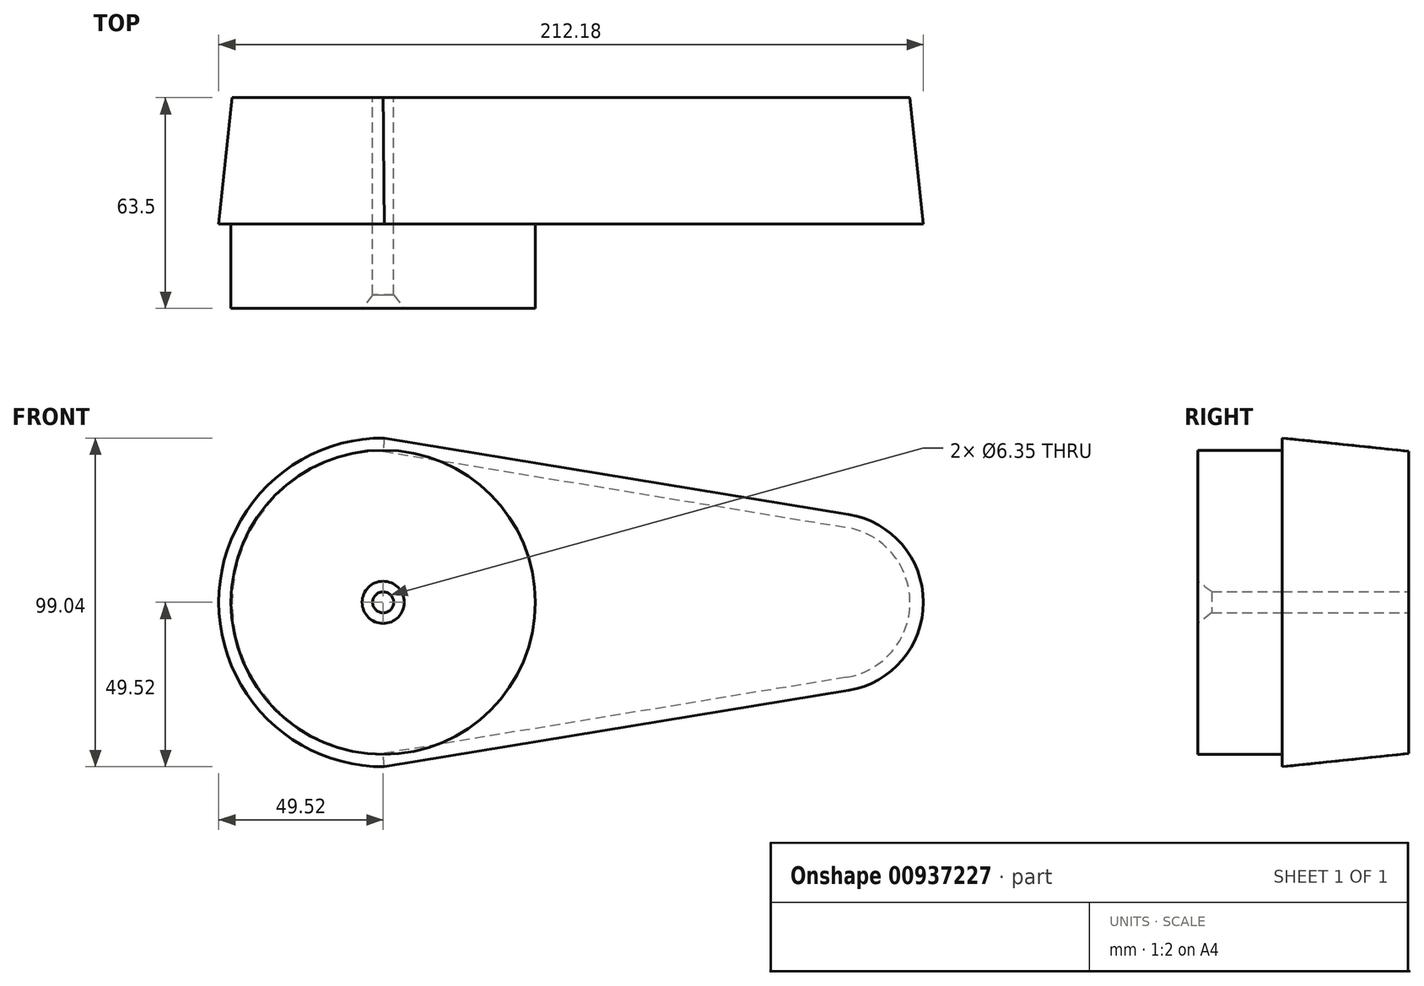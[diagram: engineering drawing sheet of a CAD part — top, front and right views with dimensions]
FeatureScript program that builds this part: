
annotation { "Feature Type Name" : "Feature", "Feature Type Description" : "" }
export const myFeature = defineFeature(function(context is Context, id is Id, definition is map)
    precondition{}
    {
        {
            var Q0;
            Q0=qCreatedBy(makeId("Front.planeOp"),FACE);
            var sketch = newSketch(context, id + "F0", { "sketchPlane" : qUnion([Q0])});
            skArc(sketch, "E0", {"start": v(139.5, -22.57) * mm, "mid": v(158.65, 0) * mm, "end": v(139.5, 22.57) * mm});
            skLineSegment(sketch, "E1", {"start": v(0, -45.52) * mm, "end": v(139.5, -22.57) * mm});
            skLineSegment(sketch, "E2", {"start": v(0, 45.52) * mm, "end": v(139.5, 22.57) * mm});
            skArc(sketch, "E3.trimOffspring", {"start": v(0, 45.52) * mm, "mid": v(-45.52, 0) * mm, "end": v(0, -45.52) * mm});
            skSolve(sketch);
        }
        {
            var Q0;
            Q0 = qSketchRegion(id + "F0", true);
            extrude(context, id + "F1", {"entities" : qUnion([Q0]), "depth" : 38.1 * mm, "offsetDistance" : 25.4 * mm, "hasDraft" : true, "draftAngle" : 6 * degree});
        }
        {
            var Q0;
            Q0=makeQuery(id+"F1.opExtrude","CAP_FACE",FACE,{"disambiguationData":[OSD([sQuery(id+"F0.wireOp",EDGE,"E0"),sQuery(id+"F0.wireOp",EDGE,"E1"),sQuery(id+"F0.wireOp",EDGE,"E2"),sQuery(id+"F0.wireOp",EDGE,"E3.trimOffspring")])],"isStart":false});
            var sketch = newSketch(context, id + "F2", { "sketchPlane" : qUnion([Q0])});
            skCircle(sketch, "E4", {"center": v(0, 0) * mm, "radius": 45.83 * mm});
            skSolve(sketch);
        }
        {
            var Q0;
            Q0=makeQuery(id+"F2.imprint","IMPRINT",FACE,{"disambiguationData":[TD([[makeQuery(id+"F2.imprint","IMPRINT",EDGE,{"derivedFrom":sQuery(id+"F2.wireOp",EDGE,"E4")}),1.0]])]});
            var Q1;
            Q1=sQuery(id+"F2.wireOp",EDGE,"E4");
            extrude(context, id + "F3", {"entities" : qUnion([Q0]), "surfaceEntities" : qUnion([Q1]), "depth" : 25.4 * mm, "offsetDistance" : 25.4 * mm});
        }
        {
            var Q0;
            Q0=makeQuery(id+"F3.opExtrude","CAP_FACE",FACE,{"disambiguationData":[OSD([sQuery(id+"F2.wireOp",EDGE,"E4")])],"isStart":false});
            var sketch = newSketch(context, id + "F4", { "sketchPlane" : qUnion([Q0])});
            skPoint(sketch, "E5", {"position": v(0, 0) * mm});
            skSolve(sketch);
        }
        {
            var Q0;
            Q0=sQuery(id+"F4.wireOp",VERTEX,"E5");
            var Q1;
            Q1=makeQuery(id+"F1.opExtrude","SWEPT_BODY",BODY,{"disambiguationData":[OSD([sQuery(id+"F0.wireOp",EDGE,"E0"),sQuery(id+"F0.wireOp",EDGE,"E1"),sQuery(id+"F0.wireOp",EDGE,"E2"),sQuery(id+"F0.wireOp",EDGE,"E3.trimOffspring")])]});
            var Q2;
            Q2=makeQuery(id+"F3.opExtrude","SWEPT_BODY",BODY,{"disambiguationData":[OSD([sQuery(id+"F2.wireOp",EDGE,"E4")])]});
            hole(context, id + "F5", {"style" : HoleStyle.C_SINK, "endStyle" : HoleEndStyle.THROUGH, "holeDiameter" : 6.35 * mm, "cSinkDiameter" : 12.7 * mm, "cSinkAngle" : 75 * degree, "majorDiameter" : 6.35 * mm, "isTappedThrough" : true, "tappedDepth" : 12.7 * mm, "tapClearance" : 3, "locations" : qUnion([Q0]), "scope" : qUnion([Q1, Q2])});
        }
    });
